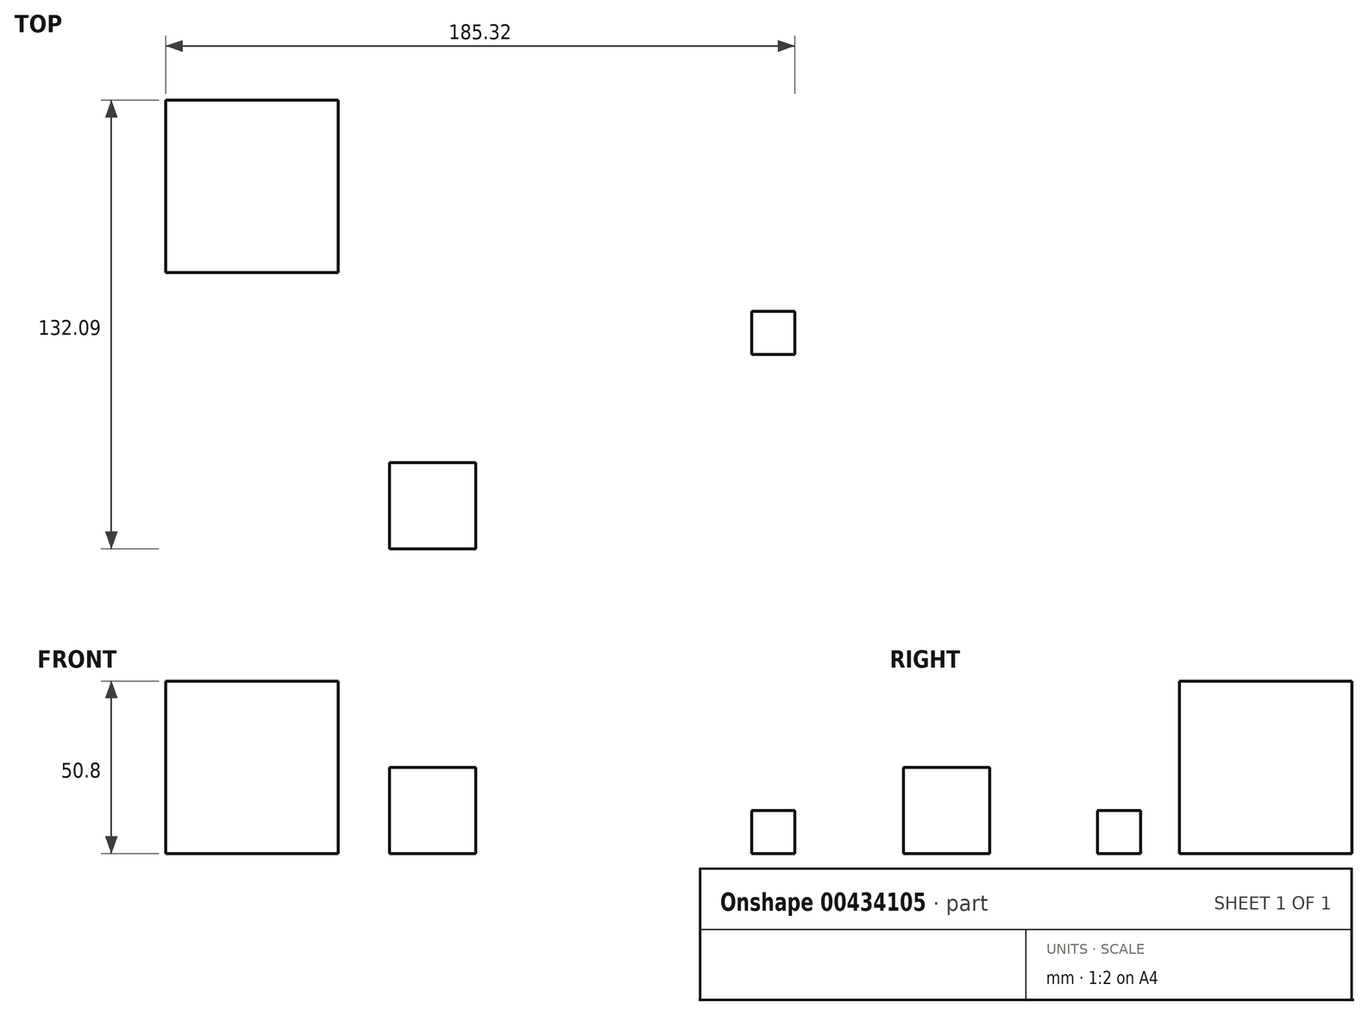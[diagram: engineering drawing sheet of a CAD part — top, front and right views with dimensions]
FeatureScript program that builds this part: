
annotation { "Feature Type Name" : "Feature", "Feature Type Description" : "" }
export const myFeature = defineFeature(function(context is Context, id is Id, definition is map)
    precondition{}
    {
        {
            var Q0;
            Q0=qCreatedBy(makeId("Top.planeOp"),FACE);
            var sketch = newSketch(context, id + "F0", { "sketchPlane" : qUnion([Q0])});
            skLineSegment(sketch, "E0.bottom", {"start": v(0, 0) * mm, "end": v(-50.8, 0) * mm});
            skLineSegment(sketch, "E0.top", {"start": v(0, 50.8) * mm, "end": v(-50.8, 50.8) * mm});
            skLineSegment(sketch, "E0.left", {"start": v(0, 0) * mm, "end": v(0, 50.8) * mm});
            skLineSegment(sketch, "E0.right", {"start": v(-50.8, 0) * mm, "end": v(-50.8, 50.8) * mm});
            skSolve(sketch);
        }
        {
            var Q0;
            Q0 = qSketchRegion(id + "F0", true);
            extrude(context, id + "F1", {"entities" : qUnion([Q0]), "depth" : 50.8 * mm});
        }
        {
            var Q0;
            Q0=qCreatedBy(makeId("Top.planeOp"),FACE);
            var sketch = newSketch(context, id + "F2", { "sketchPlane" : qUnion([Q0])});
            skLineSegment(sketch, "E1.bottom", {"start": v(15.14, -55.9) * mm, "end": v(40.54, -55.9) * mm});
            skLineSegment(sketch, "E1.top", {"start": v(15.14, -81.3) * mm, "end": v(40.54, -81.3) * mm});
            skLineSegment(sketch, "E1.left", {"start": v(15.14, -55.9) * mm, "end": v(15.14, -81.3) * mm});
            skLineSegment(sketch, "E1.right", {"start": v(40.54, -55.9) * mm, "end": v(40.54, -81.3) * mm});
            skSolve(sketch);
        }
        {
            var Q0;
            Q0 = qSketchRegion(id + "F2", true);
            extrude(context, id + "F3", {"entities" : qUnion([Q0]), "depth" : 25.4 * mm});
        }
        {
            var Q0;
            Q0=qCreatedBy(makeId("Top.planeOp"),FACE);
            var sketch = newSketch(context, id + "F4", { "sketchPlane" : qUnion([Q0])});
            skLineSegment(sketch, "E2.bottom", {"start": v(121.82, -11.4) * mm, "end": v(134.52, -11.4) * mm});
            skLineSegment(sketch, "E2.top", {"start": v(121.82, -24.1) * mm, "end": v(134.52, -24.1) * mm});
            skLineSegment(sketch, "E2.left", {"start": v(121.82, -11.4) * mm, "end": v(121.82, -24.1) * mm});
            skLineSegment(sketch, "E2.right", {"start": v(134.52, -11.4) * mm, "end": v(134.52, -24.1) * mm});
            skSolve(sketch);
        }
        {
            var Q0;
            Q0 = qSketchRegion(id + "F4", true);
            extrude(context, id + "F5", {"entities" : qUnion([Q0]), "depth" : 12.7 * mm});
        }
    });
